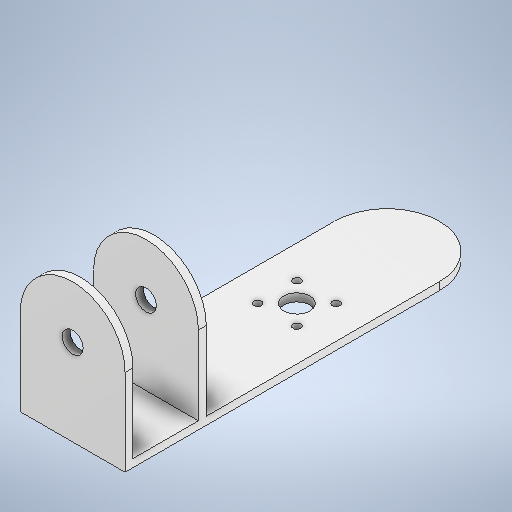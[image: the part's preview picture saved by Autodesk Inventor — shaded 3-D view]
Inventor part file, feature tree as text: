
AUTODESK INVENTOR PART (.ipt)
format: ipt  version: 2025.3 (Build 293356000, 356)  size: 283,648 bytes
history: native  units: mm
features: extrude x6, sketch x6, other x2
ambient origin geometry x8: Origin, YZ Plane, XZ Plane, XY Plane, X Axis, Y Axis, Z Axis, Center Point
bodies: Body1 (feature_tree)
feature tree (14):
  other  "Base_engine"
  other  "Sólido1"
  extrude  "Extrusión1"  Depth=80.0mm
  extrude  "Extrusión2"  Depth=3.0mm
  extrude  "Extrusión3"  Depth=3.0mm
  extrude  "Extrusión4"  Depth=3.0mm
  extrude  "Extrusión5"  Depth=40.0mm TaperAngle=0.0deg
  extrude  "Extrusión6"  Depth=40.0mm TaperAngle=0.0deg
  sketch  "Boceto1"  dims[d0=60.0mm d1=80.0mm]
  sketch  "Boceto2"  dims[d2=3.0mm d3=140.0mm]
  sketch  "Boceto3"  dims[d4=50.0mm d5=3.0mm]
  sketch  "Boceto4"  dims[d6=50.0mm d7=3.0mm]
  sketch  "Boceto5"  dims[d8=25.0mm d9=40.0mm d10=0.0mm]
  sketch  "Boceto6"  dims[d11=40.0mm d12=0.0mm d13=40.0mm d14=0.0mm d15=8.0mm d16=40.0mm d17=0.0mm d20=10.0mm d21=10.0mm d22=40.0mm d23=0.0mm d24=15.0mm d25=15.0mm d26=3.0mm d27=3.0mm d28=3.0mm d29=3.0mm d30=5.0mm d31=0.0mm]
